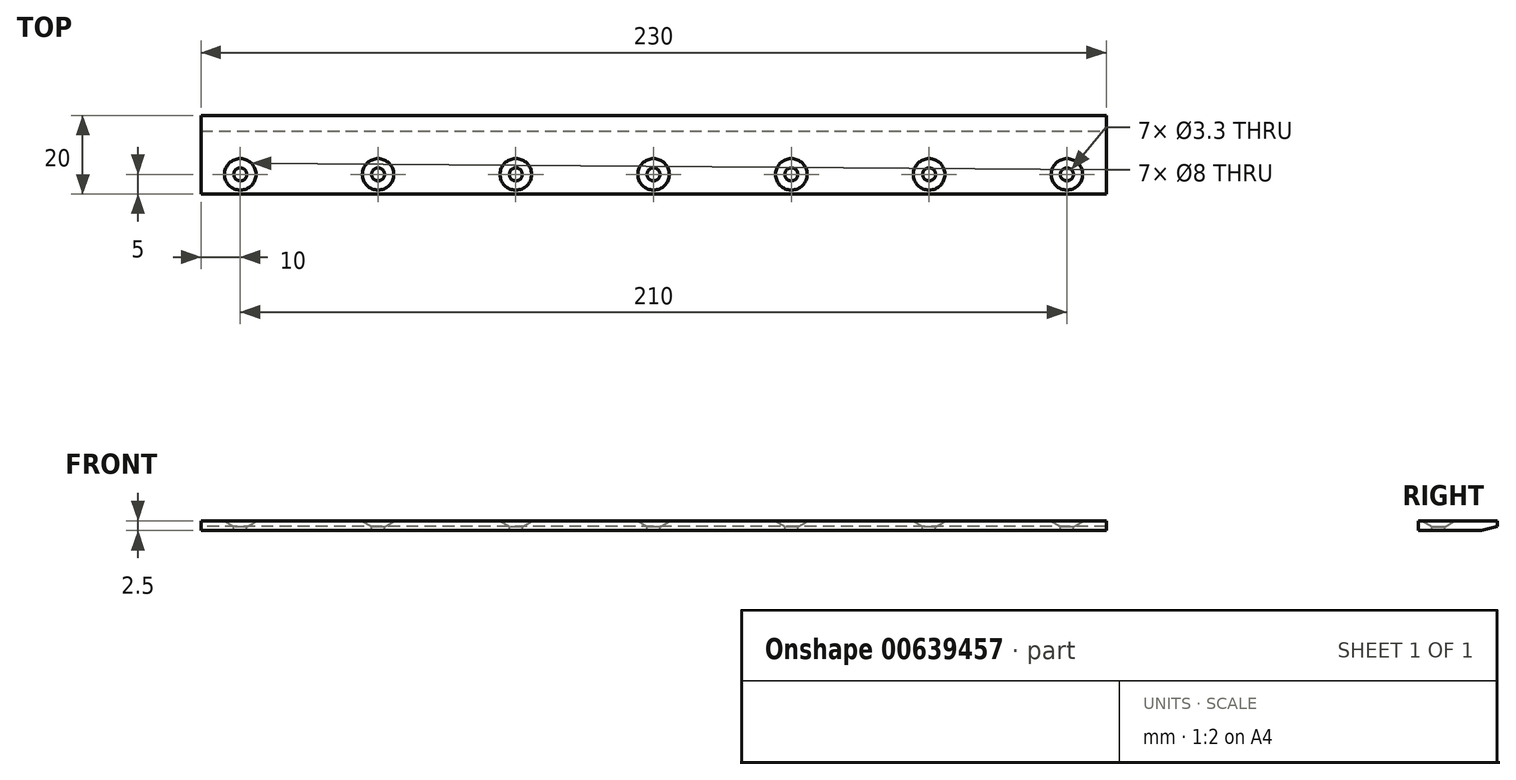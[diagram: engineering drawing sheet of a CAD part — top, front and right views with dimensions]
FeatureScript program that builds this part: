
annotation { "Feature Type Name" : "Feature", "Feature Type Description" : "" }
export const myFeature = defineFeature(function(context is Context, id is Id, definition is map)
    precondition{}
    {
        {
            var Q0;
            Q0=qCreatedBy(makeId("Top.planeOp"),FACE);
            var sketch = newSketch(context, id + "F0", { "sketchPlane" : qUnion([Q0])});
            skLineSegment(sketch, "E0.bottom", {"start": v(115, 10) * mm, "end": v(-115, 10) * mm});
            skLineSegment(sketch, "E0.top", {"start": v(115, -10) * mm, "end": v(-115, -10) * mm});
            skLineSegment(sketch, "E0.left", {"start": v(115, 10) * mm, "end": v(115, -10) * mm});
            skLineSegment(sketch, "E0.right", {"start": v(-115, 10) * mm, "end": v(-115, -10) * mm});
            skPoint(sketch, "E0.middle", {"position": v(0, 0) * mm});
            skSolve(sketch);
        }
        {
            var Q0;
            Q0=makeQuery(id+"F0.imprint","IMPRINT",FACE,{"disambiguationData":[TD([[makeQuery(id+"F0.imprint","IMPRINT",EDGE,{"derivedFrom":sQuery(id+"F0.wireOp",EDGE,"E0.bottom")}),1.0]])]});
            extrude(context, id + "F1", {"entities" : qUnion([Q0]), "depth" : 2.5 * mm, "offsetDistance" : 25 * mm});
        }
        {
            var Q0;
            Q0=makeQuery(id+"F1.opExtrude","CAP_FACE",FACE,{"disambiguationData":[OSD([sQuery(id+"F0.wireOp",EDGE,"E0.bottom"),sQuery(id+"F0.wireOp",EDGE,"E0.top"),sQuery(id+"F0.wireOp",EDGE,"E0.left"),sQuery(id+"F0.wireOp",EDGE,"E0.right")])],"isStart":false});
            var sketch = newSketch(context, id + "F2", { "sketchPlane" : qUnion([Q0])});
            skPoint(sketch, "E1", {"position": v(-105, -5) * mm});
            skPoint(sketch, "E2", {"position": v(-70, -5) * mm});
            skPoint(sketch, "E3", {"position": v(-35, -5) * mm});
            skPoint(sketch, "E4", {"position": v(0, -5) * mm});
            skPoint(sketch, "E5", {"position": v(35, -5) * mm});
            skPoint(sketch, "E6", {"position": v(70, -5) * mm});
            skPoint(sketch, "E7", {"position": v(105, -5) * mm});
            skSolve(sketch);
        }
        {
            var Q0;
            Q0=sQuery(id+"F2.wireOp",VERTEX,"E1");
            var Q1;
            Q1=sQuery(id+"F2.wireOp",VERTEX,"E2");
            var Q2;
            Q2=sQuery(id+"F2.wireOp",VERTEX,"E3");
            var Q3;
            Q3=sQuery(id+"F2.wireOp",VERTEX,"E4");
            var Q4;
            Q4=sQuery(id+"F2.wireOp",VERTEX,"E5");
            var Q5;
            Q5=sQuery(id+"F2.wireOp",VERTEX,"E7");
            var Q6;
            Q6=sQuery(id+"F2.wireOp",VERTEX,"E6");
            var Q7;
            Q7=makeQuery(id+"F1.opExtrude","SWEPT_BODY",BODY,{"disambiguationData":[OSD([sQuery(id+"F0.wireOp",EDGE,"E0.bottom"),sQuery(id+"F0.wireOp",EDGE,"E0.top"),sQuery(id+"F0.wireOp",EDGE,"E0.left"),sQuery(id+"F0.wireOp",EDGE,"E0.right")])]});
            hole(context, id + "F3", {"style" : HoleStyle.SIMPLE, "endStyle" : HoleEndStyle.THROUGH, "standardTappedOrClearance" : lookupTablePath({ "standard" : "ISO", "fit" : "Normal", "size" : "M3", "type" : "Clearance" }), "standardBlindInLast" : lookupTablePath({ "fit" : "Standard", "standard" : "ISO", "size" : "M3", "type" : "Clearance" }), "holeDiameter" : 3.3 * mm, "majorDiameter" : 5 * mm, "isTappedThrough" : true, "tappedDepth" : 12 * mm, "tapClearance" : 3, "locations" : qUnion([Q0, Q1, Q2, Q3, Q4, Q5, Q6]), "scope" : qUnion([Q7])});
        }
        {
            var Q0;
            Q0=makeQuery(id+"F1.opExtrude","CAP_EDGE",EDGE,{"disambiguationData":[OSD([sQuery(id+"F0.wireOp",EDGE,"E0.bottom")])],"isStart":true});
            chamfer(context, id + "F4", {"entities" : qUnion([Q0]), "chamferType" : ChamferType.TWO_OFFSETS, "width1" : 1 * mm, "oppositeDirection" : false, "width2" : 4 * mm, "tangentPropagation" : true});
        }
        {
            var Q0;
            Q0=makeQuery(id+"F1.opExtrude","CAP_FACE",FACE,{"disambiguationData":[OSD([sQuery(id+"F0.wireOp",EDGE,"E0.bottom"),sQuery(id+"F0.wireOp",EDGE,"E0.top"),sQuery(id+"F0.wireOp",EDGE,"E0.left"),sQuery(id+"F0.wireOp",EDGE,"E0.right")])],"isStart":false});
            var sketch = newSketch(context, id + "F5", { "sketchPlane" : qUnion([Q0])});
            skPoint(sketch, "E8", {"position": v(-105, -5) * mm});
            skPoint(sketch, "E9", {"position": v(-70, -5) * mm});
            skPoint(sketch, "E10", {"position": v(-35, -5) * mm});
            skPoint(sketch, "E11", {"position": v(0, -5) * mm});
            skPoint(sketch, "E12", {"position": v(35, -5) * mm});
            skPoint(sketch, "E13", {"position": v(70, -5) * mm});
            skPoint(sketch, "E14", {"position": v(105, -5) * mm});
            skSolve(sketch);
        }
        {
            var Q0;
            Q0=sQuery(id+"F5.wireOp",VERTEX,"E8");
            var Q1;
            Q1=sQuery(id+"F5.wireOp",VERTEX,"E9");
            var Q2;
            Q2=sQuery(id+"F5.wireOp",VERTEX,"E10");
            var Q3;
            Q3=sQuery(id+"F5.wireOp",VERTEX,"E11");
            var Q4;
            Q4=sQuery(id+"F5.wireOp",VERTEX,"E14");
            var Q5;
            Q5=sQuery(id+"F5.wireOp",VERTEX,"E13");
            var Q6;
            Q6=sQuery(id+"F5.wireOp",VERTEX,"E12");
            var Q7;
            Q7=makeQuery(id+"F1.opExtrude","SWEPT_BODY",BODY,{"disambiguationData":[OSD([sQuery(id+"F0.wireOp",EDGE,"E0.bottom"),sQuery(id+"F0.wireOp",EDGE,"E0.top"),sQuery(id+"F0.wireOp",EDGE,"E0.left"),sQuery(id+"F0.wireOp",EDGE,"E0.right")])]});
            hole(context, id + "F6", {"style" : HoleStyle.SIMPLE, "endStyle" : HoleEndStyle.BLIND, "holeDiameter" : 8 * mm, "majorDiameter" : 5 * mm, "holeDepth" : 0.2 * mm, "isTappedThrough" : true, "tappedDepth" : 12 * mm, "tapClearance" : 3, "locations" : qUnion([Q0, Q1, Q2, Q3, Q4, Q5, Q6]), "scope" : qUnion([Q7])});
        }
    });
